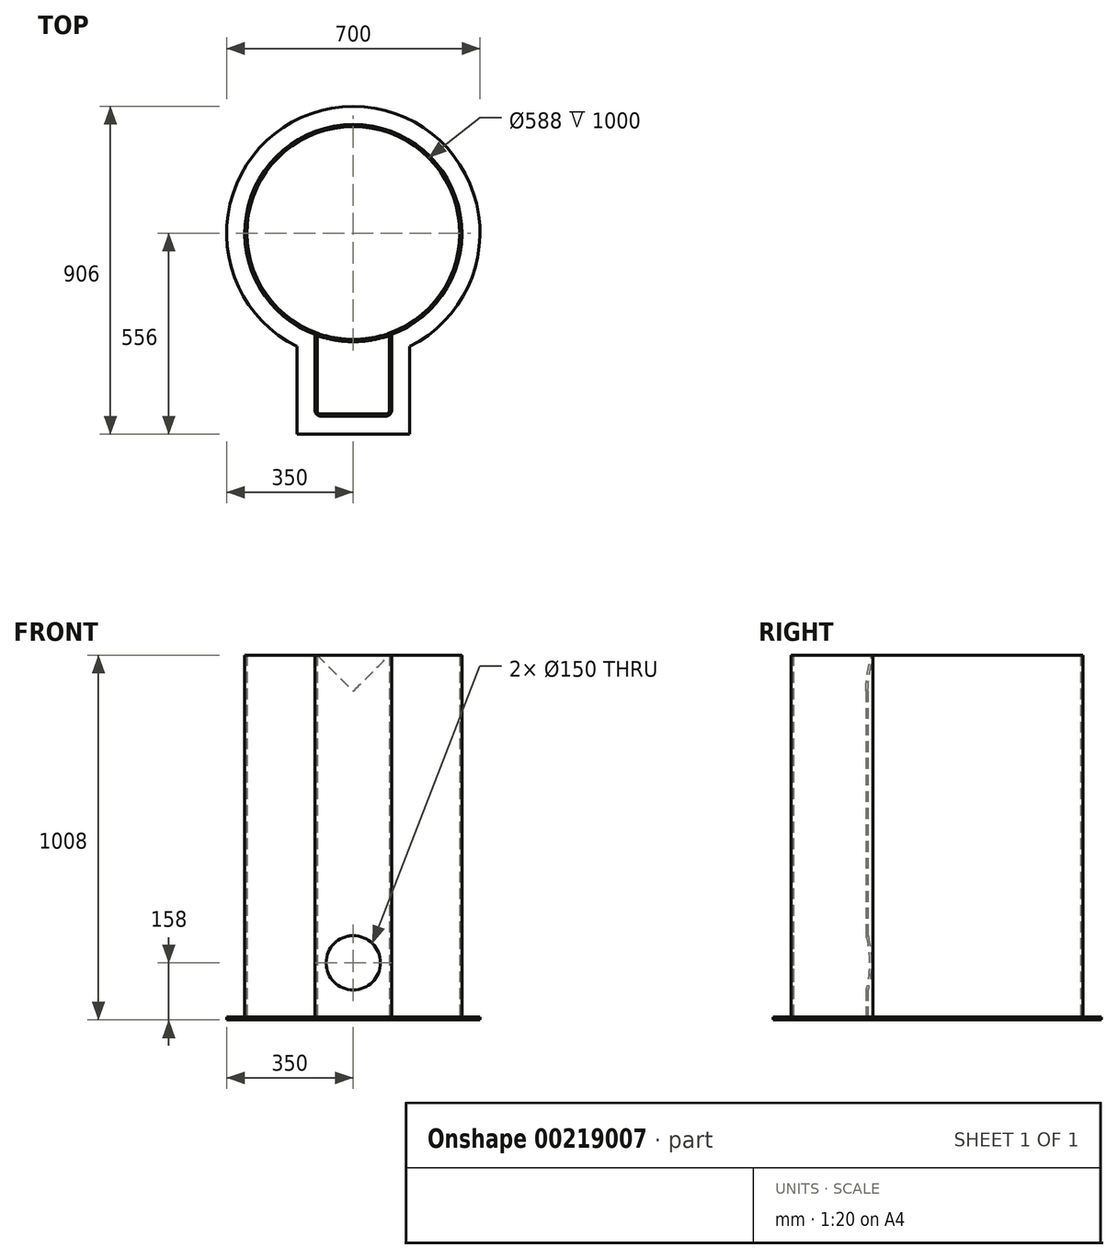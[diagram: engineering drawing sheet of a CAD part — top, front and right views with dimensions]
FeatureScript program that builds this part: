
annotation { "Feature Type Name" : "Feature", "Feature Type Description" : "" }
export const myFeature = defineFeature(function(context is Context, id is Id, definition is map)
    precondition{}
    {
        {
            var Q0;
            Q0=qCreatedBy(makeId("Top.planeOp"),FACE);
            var sketch = newSketch(context, id + "F0", { "sketchPlane" : qUnion([Q0])});
            skCircle(sketch, "E0", {"center": v(0, 0) * mm, "radius": 294 * mm});
            skCircle(sketch, "E1", {"center": v(0, 0) * mm, "radius": 300 * mm});
            skLineSegment(sketch, "E2", {"start": v(-100, -282.84) * mm, "end": v(-100, -490) * mm});
            skLineSegment(sketch, "E3", {"start": v(-90, -500) * mm, "end": v(90, -500) * mm});
            skLineSegment(sketch, "E4", {"start": v(100, -490) * mm, "end": v(100, -282.84) * mm});
            skLineSegment(sketch, "E5", {"start": v(-106, -280.65) * mm, "end": v(-106, -490) * mm});
            skLineSegment(sketch, "E6", {"start": v(-90, -506) * mm, "end": v(90, -506) * mm});
            skLineSegment(sketch, "E7", {"start": v(106, -490) * mm, "end": v(106, -280.65) * mm});
            skLineSegment(sketch, "E8", {"start": v(0, 0) * mm, "end": v(0, -408.77) * mm, "construction": true});
            skPoint(sketch, "E9.visualSharp", {"position": v(-100, -500) * mm});
            skArc(sketch, "E9.filletArc", {"start": v(-100, -490) * mm, "mid": v(-97.07, -497.07) * mm, "end": v(-90, -500) * mm});
            skPoint(sketch, "E10.visualSharp", {"position": v(100, -500) * mm});
            skArc(sketch, "E10.filletArc", {"start": v(90, -500) * mm, "mid": v(97.07, -497.07) * mm, "end": v(100, -490) * mm});
            skPoint(sketch, "E11.visualSharp", {"position": v(106, -506) * mm});
            skArc(sketch, "E11.filletArc", {"start": v(90, -506) * mm, "mid": v(101.31, -501.31) * mm, "end": v(106, -490) * mm});
            skPoint(sketch, "E12.visualSharp", {"position": v(-106, -506) * mm});
            skArc(sketch, "E12.filletArc", {"start": v(-106, -490) * mm, "mid": v(-101.31, -501.31) * mm, "end": v(-90, -506) * mm});
            skSolve(sketch);
        }
        {
            var Q0;
            Q0=makeQuery(id+"F0.imprint","IMPRINT",FACE,{"disambiguationData":[TD([[makeQuery(id+"F0.imprint","IMPRINT",EDGE,{"derivedFrom":sQuery(id+"F0.wireOp",EDGE,"E0")}),-1.0]])]});
            extrude(context, id + "F1", {"entities" : qUnion([Q0]), "depth" : 1000 * mm});
        }
        {
            var Q0;
            Q0=qCreatedBy(makeId("Front.planeOp"),FACE);
            var sketch = newSketch(context, id + "F2", { "sketchPlane" : qUnion([Q0])});
            skLineSegment(sketch, "E13", {"start": v(-100, 1000) * mm, "end": v(0, 900) * mm});
            skLineSegment(sketch, "E14", {"start": v(0, 900) * mm, "end": v(100, 1000) * mm});
            skLineSegment(sketch, "E15", {"start": v(100, 1000) * mm, "end": v(-100, 1000) * mm});
            skCircle(sketch, "E16", {"center": v(0, 150) * mm, "radius": 75 * mm});
            skSolve(sketch);
        }
        {
            var Q0;
            Q0=makeQuery(id+"F2.imprint","IMPRINT",FACE,{"disambiguationData":[TD([[makeQuery(id+"F2.imprint","IMPRINT",EDGE,{"derivedFrom":sQuery(id+"F2.wireOp",EDGE,"E13")}),1.0]])]});
            extrude(context, id + "F3", {"entities" : qUnion([Q0]), "operationType" : NewBodyOperationType.REMOVE, "endBound" : BoundingType.THROUGH_ALL, "depth" : 25 * mm});
        }
        {
            var Q0;
            {var subQ2=sQuery(id+"F0.wireOp",EDGE,"E2");Q0=makeQuery(id+"F0.imprint","IMPRINT",FACE,{"disambiguationData":[TD([[makeQuery(id+"F0.imprint","IMPRINT",EDGE,{"derivedFrom":subQ2}),-1.0]])]});}
            extrude(context, id + "F4", {"entities" : qUnion([Q0]), "depth" : 1000 * mm});
        }
        {
            var Q0;
            Q0=makeQuery(id+"F2.imprint","IMPRINT",FACE,{"disambiguationData":[TD([[makeQuery(id+"F2.imprint","IMPRINT",EDGE,{"derivedFrom":sQuery(id+"F2.wireOp",EDGE,"E16")}),1.0]])]});
            extrude(context, id + "F5", {"entities" : qUnion([Q0]), "operationType" : NewBodyOperationType.REMOVE, "endBound" : BoundingType.THROUGH_ALL, "depth" : 25 * mm});
        }
        {
            var Q0;
            Q0=makeQuery(id+"F0.imprint","IMPRINT",FACE,{"disambiguationData":[TD([[makeQuery(id+"F0.imprint","IMPRINT",EDGE,{"derivedFrom":sQuery(id+"F0.wireOp",EDGE,"E0")}),-1.0]])]});
            var sketch = newSketch(context, id + "F6", { "sketchPlane" : qUnion([Q0])});
            skCircle(sketch, "E17", {"center": v(0, 0) * mm, "radius": 350 * mm});
            skLineSegment(sketch, "E18", {"start": v(-156, -313.31) * mm, "end": v(-156, -556) * mm});
            skLineSegment(sketch, "E19", {"start": v(-156, -556) * mm, "end": v(156, -556) * mm});
            skLineSegment(sketch, "E20", {"start": v(156, -556) * mm, "end": v(156, -313.31) * mm});
            skSolve(sketch);
        }
        {
            var Q0;
            {var subQ4=sQuery(id+"F6.wireOp",EDGE,"E17");var subQ5=makeQuery(id+"F6.imprint","INTERSECT",VERTEX,{"derivedFrom":[subQ4,sQuery(id+"F6.wireOp",EDGE,"E18")]});Q0=makeQuery(id+"F6.imprint","IMPRINT",FACE,{"disambiguationData":[TD([[makeQuery(id+"F6.imprint","IMPRINT",EDGE,{"disambiguationData":[TD([[subQ5,-1.0]])],"derivedFrom":subQ4}),1.0]])]});}
            var Q1;
            Q1=makeQuery(id+"F6.imprint","IMPRINT",FACE,{"disambiguationData":[TD([[makeQuery(id+"F6.imprint","IMPRINT",EDGE,{"derivedFrom":makeQuery(id+"F0.imprint","IMPRINT",EDGE,{"derivedFrom":sQuery(id+"F0.wireOp",EDGE,"E0")})}),1.0]])]});
            var Q2;
            Q2=makeQuery(id+"F6.imprint","IMPRINT",FACE,{"disambiguationData":[TD([[makeQuery(id+"F6.imprint","IMPRINT",EDGE,{"derivedFrom":makeQuery(id+"F0.imprint","IMPRINT",EDGE,{"derivedFrom":sQuery(id+"F0.wireOp",EDGE,"E0")})}),-1.0]])]});
            var Q3;
            {var subQ0=sQuery(id+"F6.wireOp",EDGE,"E18");Q3=makeQuery(id+"F6.imprint","IMPRINT",FACE,{"disambiguationData":[TD([[makeQuery(id+"F6.imprint","IMPRINT",EDGE,{"derivedFrom":subQ0}),1.0]])]});}
            extrude(context, id + "F7", {"entities" : qUnion([Q0, Q1, Q2, Q3]), "oppositeDirection" : true, "depth" : 8 * mm});
        }
    });
